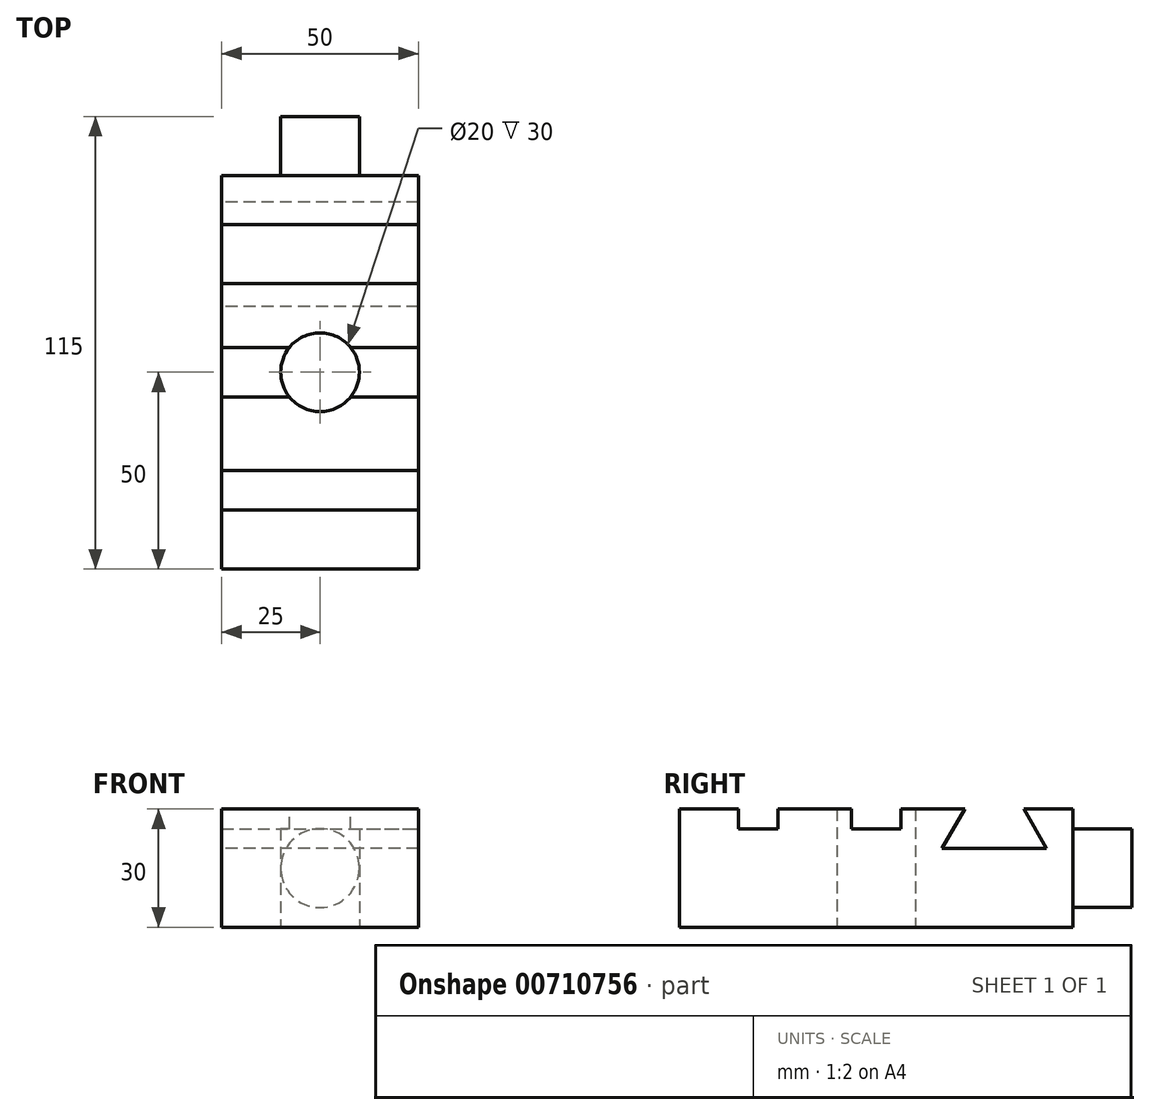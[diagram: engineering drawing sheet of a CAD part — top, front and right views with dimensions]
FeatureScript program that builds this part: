
annotation { "Feature Type Name" : "Feature", "Feature Type Description" : "" }
export const myFeature = defineFeature(function(context is Context, id is Id, definition is map)
    precondition{}
    {
        {
            var Q0;
            Q0=qCreatedBy(makeId("Top.planeOp"),FACE);
            var sketch = newSketch(context, id + "F0", { "sketchPlane" : qUnion([Q0])});
            skLineSegment(sketch, "E0.bottom", {"start": v(25, 50) * mm, "end": v(-25, 50) * mm});
            skLineSegment(sketch, "E0.top", {"start": v(25, -50) * mm, "end": v(-25, -50) * mm});
            skLineSegment(sketch, "E0.left", {"start": v(25, 50) * mm, "end": v(25, -50) * mm});
            skLineSegment(sketch, "E0.right", {"start": v(-25, 50) * mm, "end": v(-25, -50) * mm});
            skPoint(sketch, "E0.middle", {"position": v(0, 0) * mm});
            skCircle(sketch, "E1", {"center": v(0, 0) * mm, "radius": 10 * mm});
            skSolve(sketch);
        }
        {
            var Q0;
            Q0=makeQuery(id+"F0.imprint","IMPRINT",FACE,{"disambiguationData":[TD([[makeQuery(id+"F0.imprint","IMPRINT",EDGE,{"derivedFrom":sQuery(id+"F0.wireOp",EDGE,"E0.bottom")}),1.0]])]});
            extrude(context, id + "F1", {"entities" : qUnion([Q0]), "depth" : 30 * mm, "offsetDistance" : 25 * mm});
        }
        {
            var Q0;
            Q0=makeQuery(id+"F1.opExtrude","CAP_FACE",FACE,{"disambiguationData":[OSD([sQuery(id+"F0.wireOp",EDGE,"E0.bottom"),sQuery(id+"F0.wireOp",EDGE,"E0.top"),sQuery(id+"F0.wireOp",EDGE,"E0.left"),sQuery(id+"F0.wireOp",EDGE,"E0.right"),sQuery(id+"F0.wireOp",EDGE,"E1")])],"isStart":false});
            var sketch = newSketch(context, id + "F2", { "sketchPlane" : qUnion([Q0])});
            skLineSegment(sketch, "E2.bottom", {"start": v(-25, -25) * mm, "end": v(25, -25) * mm});
            skLineSegment(sketch, "E2.top", {"start": v(-25, -35) * mm, "end": v(25, -35) * mm});
            skLineSegment(sketch, "E2.left", {"start": v(-25, -25) * mm, "end": v(-25, -35) * mm});
            skLineSegment(sketch, "E2.right", {"start": v(25, -25) * mm, "end": v(25, -35) * mm});
            skLineSegment(sketch, "E3", {"start": v(-25, 6.25) * mm, "end": v(25, 6.25) * mm});
            skLineSegment(sketch, "E4", {"start": v(-25, -6.25) * mm, "end": v(25, -6.25) * mm});
            skPoint(sketch, "E5", {"position": v(0, 0) * mm});
            skLineSegment(sketch, "E6", {"start": v(-25, -6.25) * mm, "end": v(-25, 6.25) * mm});
            skLineSegment(sketch, "E7", {"start": v(25, -6.25) * mm, "end": v(25, 6.25) * mm});
            skLineSegment(sketch, "E8", {"start": v(-25, 0) * mm, "end": v(25, 0) * mm, "construction": true});
            skSolve(sketch);
        }
        {
            var Q0;
            {var subQ0=sQuery(id+"F2.wireOp",EDGE,"E7");Q0=makeQuery(id+"F2.imprint","IMPRINT",FACE,{"disambiguationData":[TD([[makeQuery(id+"F2.imprint","IMPRINT",EDGE,{"derivedFrom":subQ0}),-1.0]])]});}
            var Q1;
            Q1=makeQuery(id+"F2.imprint","IMPRINT",FACE,{"disambiguationData":[TD([[makeQuery(id+"F2.imprint","IMPRINT",EDGE,{"derivedFrom":sQuery(id+"F2.wireOp",EDGE,"E2.bottom")}),-1.0]])]});
            var Q2;
            {var subQ0=sQuery(id+"F2.wireOp",EDGE,"E6");Q2=makeQuery(id+"F2.imprint","IMPRINT",FACE,{"disambiguationData":[TD([[makeQuery(id+"F2.imprint","IMPRINT",EDGE,{"derivedFrom":subQ0}),1.0]])]});}
            extrude(context, id + "F3", {"entities" : qUnion([Q0, Q1, Q2]), "operationType" : NewBodyOperationType.REMOVE, "oppositeDirection" : true, "depth" : 5 * mm, "offsetDistance" : 25 * mm});
        }
        {
            var Q0;
            Q0=makeQuery(id+"F1.opExtrude","SWEPT_FACE",FACE,{"disambiguationData":[OSD([sQuery(id+"F0.wireOp",EDGE,"E0.right")])]});
            var sketch = newSketch(context, id + "F4", { "sketchPlane" : qUnion([Q0])});
            skLineSegment(sketch, "E9", {"start": v(-37.5, 30) * mm, "end": v(-43.27, 20) * mm});
            skLineSegment(sketch, "E10", {"start": v(-43.27, 20) * mm, "end": v(-16.73, 20) * mm});
            skLineSegment(sketch, "E11", {"start": v(-16.73, 20) * mm, "end": v(-22.5, 30) * mm});
            skLineSegment(sketch, "E12", {"start": v(-22.5, 30) * mm, "end": v(-37.5, 30) * mm});
            skLineSegment(sketch, "E13", {"start": v(-30, 20) * mm, "end": v(-30, 30) * mm, "construction": true});
            skSolve(sketch);
        }
        {
            var Q0;
            Q0=makeQuery(id+"F4.imprint","IMPRINT",FACE,{"disambiguationData":[TD([[makeQuery(id+"F4.imprint","IMPRINT",EDGE,{"derivedFrom":sQuery(id+"F4.wireOp",EDGE,"E9")}),1.0]])]});
            extrude(context, id + "F5", {"entities" : qUnion([Q0]), "operationType" : NewBodyOperationType.REMOVE, "endBound" : BoundingType.UP_TO_NEXT, "oppositeDirection" : true, "depth" : 38.6 * mm, "offsetDistance" : 25 * mm});
        }
        {
            var Q0;
            Q0=makeQuery(id+"F1.opExtrude","SWEPT_FACE",FACE,{"disambiguationData":[OSD([sQuery(id+"F0.wireOp",EDGE,"E0.bottom")])]});
            var sketch = newSketch(context, id + "F6", { "sketchPlane" : qUnion([Q0])});
            skCircle(sketch, "E14", {"center": v(0, 15) * mm, "radius": 10 * mm});
            skPoint(sketch, "E14.centerSnap0", {"position": v(-25, 15) * mm});
            skPoint(sketch, "E14.centerSnap1", {"position": v(0, 30) * mm});
            skSolve(sketch);
        }
        {
            var Q0;
            Q0=makeQuery(id+"F6.imprint","IMPRINT",FACE,{"disambiguationData":[TD([[makeQuery(id+"F6.imprint","IMPRINT",EDGE,{"derivedFrom":sQuery(id+"F6.wireOp",EDGE,"E14")}),1.0]])]});
            extrude(context, id + "F7", {"entities" : qUnion([Q0]), "operationType" : NewBodyOperationType.ADD, "depth" : 15 * mm, "offsetDistance" : 25 * mm});
        }
    });
